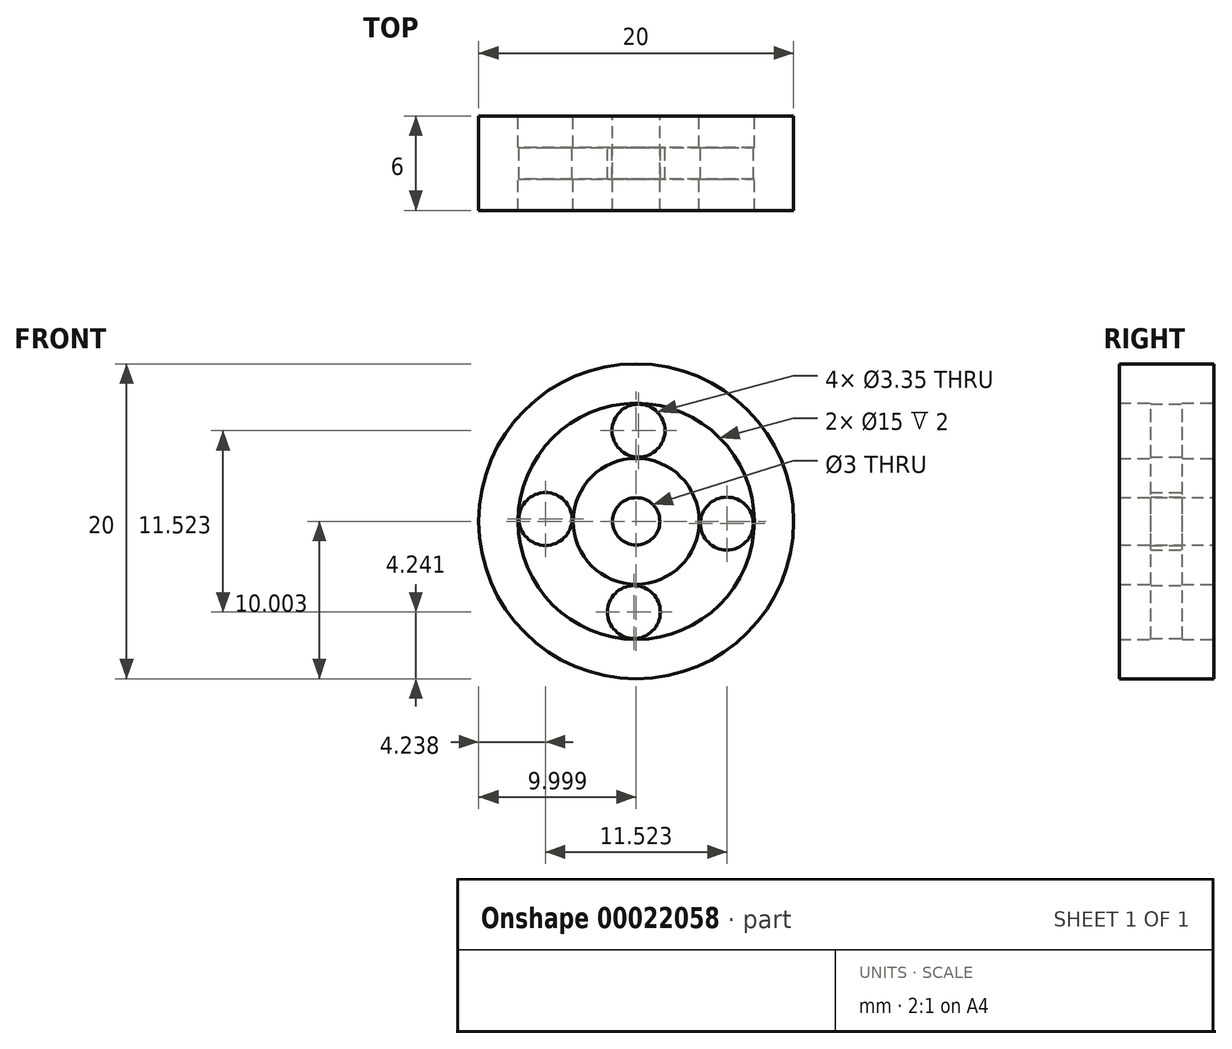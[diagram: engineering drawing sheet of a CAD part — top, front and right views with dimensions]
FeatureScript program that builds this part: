
annotation { "Feature Type Name" : "Feature", "Feature Type Description" : "" }
export const myFeature = defineFeature(function(context is Context, id is Id, definition is map)
    precondition{}
    {
        {
            var Q0;
            Q0=qCreatedBy(makeId("Front.planeOp"),FACE);
            var sketch = newSketch(context, id + "F0", { "sketchPlane" : qUnion([Q0])});
            skPoint(sketch, "E0.center", {"position": v(-11.85, 11.42) * mm});
            skCircle(sketch, "E1", {"center": v(-7.76, 25.41) * mm, "radius": 10 * mm});
            skCircle(sketch, "E2", {"center": v(-7.76, 25.41) * mm, "radius": 7.5 * mm});
            skCircle(sketch, "E3", {"center": v(-7.76, 25.41) * mm, "radius": 4 * mm});
            skCircle(sketch, "E4", {"center": v(-7.76, 25.41) * mm, "radius": 1.5 * mm});
            skCircle(sketch, "E5", {"center": v(-7.62, 31.17) * mm, "radius": 1.68 * mm});
            skCircle(sketch, "E6.1.0", {"center": v(-13.52, 25.56) * mm, "radius": 1.68 * mm});
            skCircle(sketch, "E6.2.0", {"center": v(-7.9, 19.65) * mm, "radius": 1.68 * mm});
            skCircle(sketch, "E6.3.0", {"center": v(-2, 25.27) * mm, "radius": 1.68 * mm});
            skSolve(sketch);
        }
        {
            var Q0;
            Q0=makeQuery(id+"F0.imprint","IMPRINT",FACE,{"disambiguationData":[TD([[makeQuery(id+"F0.imprint","IMPRINT",EDGE,{"derivedFrom":sQuery(id+"F0.wireOp",EDGE,"E1")}),1.0]])]});
            extrude(context, id + "F1", {"entities" : qUnion([Q0]), "endBound" : BoundingType.SYMMETRIC, "depth" : 6 * mm});
        }
        {
            var Q0;
            Q0=makeQuery(id+"F0.imprint","IMPRINT",FACE,{"disambiguationData":[TD([[makeQuery(id+"F0.imprint","IMPRINT",EDGE,{"derivedFrom":sQuery(id+"F0.wireOp",EDGE,"E2")}),1.0]])]});
            extrude(context, id + "F2", {"entities" : qUnion([Q0]), "operationType" : NewBodyOperationType.ADD, "endBound" : BoundingType.SYMMETRIC, "depth" : 2 * mm});
        }
        {
            var Q0;
            Q0=makeQuery(id+"F0.imprint","IMPRINT",FACE,{"disambiguationData":[TD([[makeQuery(id+"F0.imprint","IMPRINT",EDGE,{"derivedFrom":sQuery(id+"F0.wireOp",EDGE,"E3")}),1.0]])]});
            extrude(context, id + "F3", {"entities" : qUnion([Q0]), "operationType" : NewBodyOperationType.ADD, "endBound" : BoundingType.SYMMETRIC, "depth" : 6 * mm});
        }
    });
